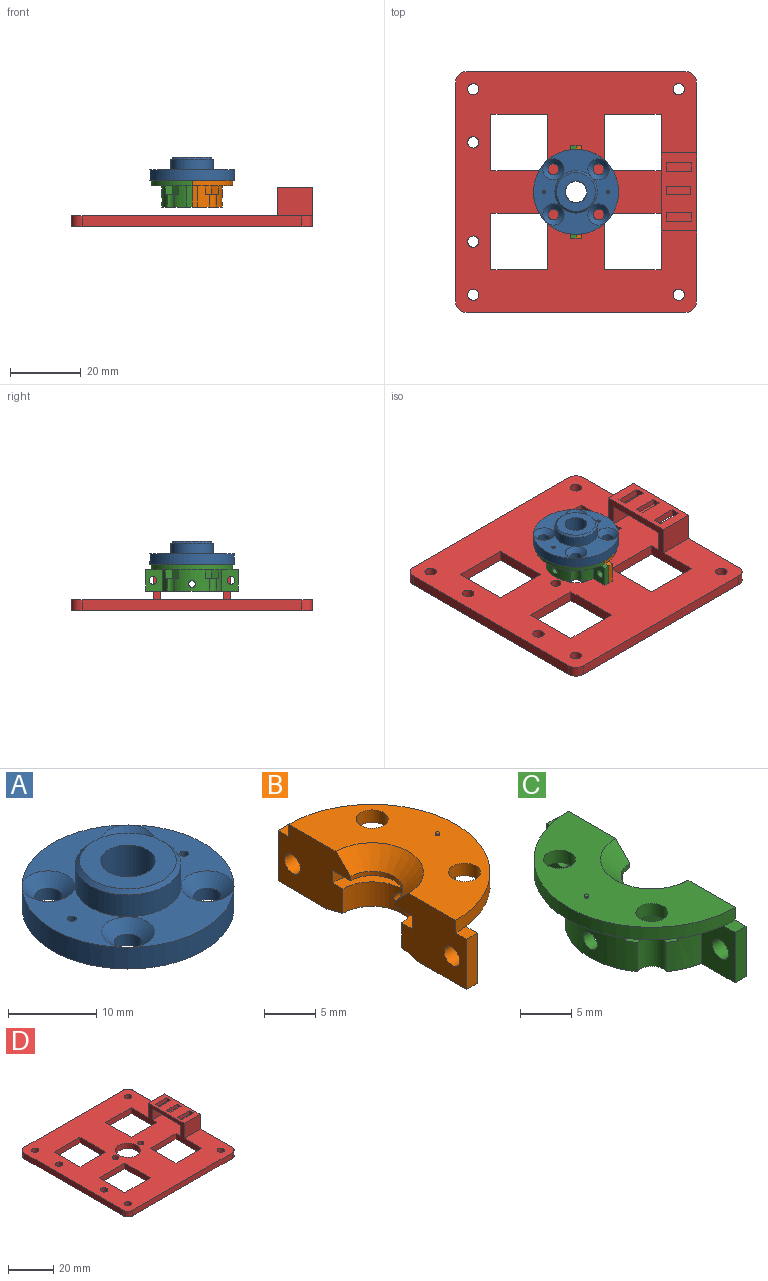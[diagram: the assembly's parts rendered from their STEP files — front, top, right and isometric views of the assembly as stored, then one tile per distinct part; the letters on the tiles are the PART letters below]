
ASSEMBLY  parts=4 mates=4
PART A: 18 faces, bbox 24x24x6.5 mm
  f0: cylinder r=3.1mm len=6.2mm, axis (0,0,-1), area 116.9mm2, adj f11,f13
  f1: cylinder r=1.6mm len=3.2mm, axis (0,0,-1), area 16.1mm2, adj f9,f17
  f2: cylinder r=1.6mm len=3.2mm, axis (0,0,-1), area 16.1mm2, adj f9,f16
  f3: cylinder r=1.6mm len=3.2mm, axis (0,0,-1), area 16.1mm2, adj f9,f15
  f4: cylinder r=1.6mm len=3.2mm, axis (0,0,-1), area 16.1mm2, adj f9,f14
  f5: cylinder r=0.5mm len=3mm, axis (0,0,-1), area 9.4mm2, adj f8,f9
  f6: cylinder r=0.5mm len=3mm, axis (0,0,-1), area 9.4mm2, adj f8,f9
  f7: cylinder r=12mm len=24mm, axis (0,0,-1), area 226.2mm2, adj f8,f9
  f8: plane 24x24mm, normal (0,0,1), area 225.6mm2, adj f5,f6,f7,f10,f14,f15,f16,f17
  f9: plane 24x24mm, normal (0,0,-1), area 377.9mm2, adj f1,f2,f3,f4,f5,f6,f7,f13
  f10: cylinder r=5.98mm len=11.95mm, axis (0,0,-1), area 112.6mm2, adj f8,f12
  f11: plane 10.95x10.95mm, normal (0,0,1), area 64mm2, adj f0,f12
  f12: cone r=5.47mm half-angle=45deg, axis (0,0,-1), area 25.4mm2, adj f10,f11
  f13: cone r=3.6mm half-angle=45deg, axis (0,0,-1), area 14.9mm2, adj f0,f9
  f14: cone r=1.6mm half-angle=45deg, axis (0,0,1), area 28.6mm2, adj f4,f8
  f15: cone r=1.6mm half-angle=45deg, axis (0,0,1), area 28.6mm2, adj f3,f8
  f16: cone r=1.6mm half-angle=45deg, axis (0,0,1), area 28.6mm2, adj f2,f8
  f17: cone r=1.6mm half-angle=45deg, axis (0,0,1), area 28.6mm2, adj f1,f8
PART B: 47 faces, bbox 11.5x26x7.9 mm
  f0: plane 4.29x4.29mm, normal (0,0,1), area 7.1mm2, adj f6,f7,f8,f14,f15,f16
  f1: plane 4.29x4.29mm, normal (0,0,1), area 7.1mm2, adj f3,f4,f5,f16,f17,f18
  f2: cylinder r=0.95mm len=1.9mm, axis (-1,0,0), area 7.3mm2, adj f16,f19
  f3: plane 2.5x2.04mm, normal (0.97,-0.26,0), area 5.3mm2, adj f1,f4,f18,f20
  f4: plane 2.5x2.25mm, normal (0.71,0.71,0), area 7.9mm2, adj f1,f3,f5,f20
  f5: plane 2.5x2.04mm, normal (-0.26,0.97,0), area 5.3mm2, adj f1,f4,f16,f20
  f6: plane 2.5x2.04mm, normal (-0.26,-0.97,0), area 5.3mm2, adj f0,f7,f16,f20
  f7: plane 2.5x2.25mm, normal (0.71,-0.71,0), area 7.9mm2, adj f0,f6,f8,f20
  f8: plane 2.5x2.04mm, normal (0.97,0.26,0), area 5.3mm2, adj f0,f7,f14,f20
  f9: cone r=0.2mm half-angle=45deg, axis (0,0,-1), area 0.2mm2, adj f23
  f10: cylinder r=0.95mm len=1.9mm, axis (-1,0,0), area 8.7mm2, adj f26,f40
  f11: plane 2.31x2.07mm, normal (0,0.87,-0.5), area 4.9mm2, adj f12,f19,f24,f26,f39
  f12: plane 2.37x1.88mm, normal (0,0,-1), area 4.2mm2, adj f11,f13,f19,f39
  f13: plane 2.31x2.07mm, normal (0,-0.87,-0.5), area 4.9mm2, adj f12,f19,f25,f26,f39
  f14: cylinder r=8.5mm len=6mm, axis (0,0,-1), area 19.3mm2, adj f0,f8,f15,f20,f37,f43
  f15: cylinder r=1.55mm len=3.5mm, axis (0,0,1), area 12.6mm2, adj f0,f14,f16,f37
  f16: cylinder r=8.5mm len=9.84mm, axis (0,0,-1), area 53.8mm2, adj f0,f1,f2,f5,f6,f15,f17,f20
  f17: cylinder r=1.55mm len=3.5mm, axis (0,0,1), area 12.6mm2, adj f1,f16,f18,f37
  f18: cylinder r=8.5mm len=6mm, axis (0,0,-1), area 19.3mm2, adj f1,f3,f17,f20,f37,f41
  f19: plane 4.73x4.05mm, normal (-1,0,0), area 13.9mm2, adj f2,f11,f12,f13,f24,f25,f37
  f20: plane 22.8x10mm, normal (0,0,-1), area 88.6mm2, adj f3,f4,f5,f6,f7,f8,f14,f16
  f21: cylinder r=1.55mm len=3.1mm, axis (0,0,1), area 14.6mm2, adj f20,f34
  f22: cylinder r=1.55mm len=3.1mm, axis (0,0,1), area 14.6mm2, adj f20,f34
  f23: cylinder r=0.2mm len=0.4mm, axis (0,0,-1), area 0.3mm2, adj f9,f34
  f24: plane 2.31x2.02mm, normal (0,1,0), area 4.5mm2, adj f11,f19,f26,f27,f37
  f25: plane 2.31x2.02mm, normal (0,-1,0), area 4.5mm2, adj f13,f19,f26,f27,f37
  f26: cylinder r=5.5mm len=4.73mm, axis (0,0,1), area 11.9mm2, adj f10,f11,f13,f24,f25,f27,f38
  f27: cone r=5.5mm half-angle=75.1deg, axis (0,0,-1), area 33mm2, adj f24,f25,f26,f37,f40,f45,f46
  f28: plane 1.6x1.5mm, normal (0,0,1), area 2.3mm2, adj f29,f35,f41,f45
  f29: plane 6x1.5mm, normal (0,1,0), area 9mm2, adj f28,f37,f41,f45
  f30: plane 1.6x1.5mm, normal (0,0,1), area 2.3mm2, adj f31,f35,f43,f46
  f31: plane 6x1.5mm, normal (0,-1,0), area 9mm2, adj f30,f37,f43,f46
  f32: cone r=3mm half-angle=45deg, axis (0,0,1), area 35.5mm2, adj f33,f34,f45,f46
  f33: cylinder r=3mm len=6mm, axis (0,0,1), area 4.7mm2, adj f32,f36,f45,f46
  f34: plane 23x11.5mm, normal (0,0,1), area 153.2mm2, adj f21,f22,f23,f32,f35,f45,f46
  f35: cylinder r=11.5mm len=23mm, axis (0,0,-1), area 54.2mm2, adj f20,f28,f30,f34,f45,f46
  f36: plane 11x5.5mm, normal (0,0,-1), area 33.4mm2, adj f33,f39,f45,f46
  f37: plane 26x8.5mm, normal (0,0,-1), area 56mm2, adj f14,f15,f16,f17,f18,f19,f24,f25
  f38: plane 11x5.5mm, normal (0,0,1), area 21.8mm2, adj f26,f39,f40,f45,f46
  f39: cylinder r=5.5mm len=11mm, axis (0,0,-1), area 24.4mm2, adj f11,f12,f13,f36,f38,f45,f46
  f40: cylinder r=4.05mm len=8.1mm, axis (0,0,1), area 34.2mm2, adj f10,f27,f38,f45,f46
  f41: plane 6x4.63mm, normal (1,0,0), area 24mm2, adj f18,f20,f28,f29,f37,f42
  f42: cylinder r=1.1mm len=2.2mm, axis (-1,0,0), area 10.4mm2, adj f41,f45
  f43: plane 6x4.63mm, normal (1,0,0), area 24mm2, adj f14,f20,f30,f31,f37,f44
  f44: cylinder r=1.1mm len=2.2mm, axis (-1,0,0), area 10.4mm2, adj f43,f46
  f45: plane 10x7.5mm, normal (-1,0,0), area 58.9mm2, adj f27,f28,f29,f32,f33,f34,f35,f36
  f46: plane 10x7.5mm, normal (-1,0,0), area 58.9mm2, adj f27,f30,f31,f32,f33,f34,f35,f36
PART C: 47 faces, bbox 11.5x26x7.9 mm
  f0: cylinder r=4.05mm len=8.1mm, axis (0,0,1), area 34.2mm2, adj f6,f7,f29,f45,f46
  f1: cylinder r=5.5mm len=11mm, axis (0,0,-1), area 24.4mm2, adj f3,f7,f23,f24,f25,f45,f46
  f2: plane 26x8.5mm, normal (0,0,-1), area 56mm2, adj f6,f9,f11,f17,f20,f21,f22,f26
  f3: plane 11x5.5mm, normal (0,0,-1), area 33.4mm2, adj f1,f8,f45,f46
  f4: cylinder r=11.5mm len=23mm, axis (0,0,-1), area 54.2mm2, adj f5,f10,f12,f16,f45,f46
  f5: plane 23x11.5mm, normal (0,0,1), area 153.2mm2, adj f4,f13,f18,f19,f43,f45,f46
  f6: cone r=5.5mm half-angle=75.1deg, axis (0,0,-1), area 33mm2, adj f0,f2,f26,f27,f28,f45,f46
  f7: plane 11x5.5mm, normal (0,0,1), area 21.8mm2, adj f0,f1,f28,f45,f46
  f8: cylinder r=3mm len=6mm, axis (0,0,1), area 4.7mm2, adj f3,f13,f45,f46
  f9: plane 6x1.5mm, normal (0,1,0), area 9mm2, adj f2,f10,f41,f45
  f10: plane 1.6x1.5mm, normal (0,0,1), area 2.3mm2, adj f4,f9,f41,f45
  f11: plane 6x1.5mm, normal (0,-1,0), area 9mm2, adj f2,f12,f42,f46
  f12: plane 1.6x1.5mm, normal (0,0,1), area 2.3mm2, adj f4,f11,f42,f46
  f13: cone r=3mm half-angle=45deg, axis (0,0,1), area 35.5mm2, adj f5,f8,f45,f46
  f14: cylinder r=1.1mm len=2.2mm, axis (-1,0,0), area 10.4mm2, adj f42,f46
  f15: cylinder r=1.1mm len=2.2mm, axis (-1,0,0), area 10.4mm2, adj f41,f45
  f16: plane 22.8x10mm, normal (0,0,-1), area 88.6mm2, adj f4,f17,f18,f19,f20,f21,f33,f34
  f17: cylinder r=8.5mm len=6mm, axis (0,0,-1), area 19.3mm2, adj f2,f16,f32,f34,f35,f42
  f18: cylinder r=1.55mm len=3.1mm, axis (0,0,1), area 14.6mm2, adj f5,f16
  f19: cylinder r=1.55mm len=3.1mm, axis (0,0,1), area 14.6mm2, adj f5,f16
  f20: cylinder r=8.5mm len=9.84mm, axis (0,0,-1), area 53.8mm2, adj f2,f16,f30,f31,f32,f33,f35,f38
  f21: cylinder r=8.5mm len=6mm, axis (0,0,-1), area 19.3mm2, adj f2,f16,f31,f37,f39,f41
  f22: plane 4.73x4.05mm, normal (1,0,0), area 13.9mm2, adj f2,f23,f24,f25,f26,f27,f30
  f23: plane 2.31x2.07mm, normal (0,0.87,-0.5), area 4.9mm2, adj f1,f22,f25,f26,f28
  f24: plane 2.31x2.07mm, normal (0,-0.87,-0.5), area 4.9mm2, adj f1,f22,f25,f27,f28
  f25: plane 2.37x1.88mm, normal (0,0,-1), area 4.2mm2, adj f1,f22,f23,f24
  f26: plane 2.31x2.02mm, normal (0,1,0), area 4.5mm2, adj f2,f6,f22,f23,f28
  f27: plane 2.31x2.02mm, normal (0,-1,0), area 4.5mm2, adj f2,f6,f22,f24,f28
  f28: cylinder r=5.5mm len=4.73mm, axis (0,0,1), area 11.9mm2, adj f6,f7,f23,f24,f26,f27,f29
  f29: cylinder r=0.95mm len=1.9mm, axis (-1,0,0), area 8.7mm2, adj f0,f28
  f30: cylinder r=0.95mm len=1.9mm, axis (-1,0,0), area 7.3mm2, adj f20,f22
  f31: cylinder r=1.55mm len=3.5mm, axis (0,0,1), area 12.6mm2, adj f2,f20,f21,f39
  f32: cylinder r=1.55mm len=3.5mm, axis (0,0,1), area 12.6mm2, adj f2,f17,f20,f35
  f33: plane 2.5x2.04mm, normal (0.26,-0.97,0), area 5.3mm2, adj f16,f20,f35,f36
  f34: plane 2.5x2.04mm, normal (-0.97,0.26,0), area 5.3mm2, adj f16,f17,f35,f36
  f35: plane 4.29x4.29mm, normal (0,0,1), area 7.1mm2, adj f17,f20,f32,f33,f34,f36
  f36: plane 2.5x2.25mm, normal (-0.71,-0.71,0), area 7.9mm2, adj f16,f33,f34,f35
  f37: plane 2.5x2.04mm, normal (-0.97,-0.26,0), area 5.3mm2, adj f16,f21,f39,f40
  f38: plane 2.5x2.04mm, normal (0.26,0.97,0), area 5.3mm2, adj f16,f20,f39,f40
  f39: plane 4.29x4.29mm, normal (0,0,1), area 7.1mm2, adj f20,f21,f31,f37,f38,f40
  f40: plane 2.5x2.25mm, normal (-0.71,0.71,0), area 7.9mm2, adj f16,f37,f38,f39
  f41: plane 6x4.63mm, normal (-1,0,0), area 24mm2, adj f2,f9,f10,f15,f16,f21
  f42: plane 6x4.63mm, normal (-1,0,0), area 24mm2, adj f2,f11,f12,f14,f16,f17
  f43: cylinder r=0.2mm len=0.4mm, axis (0,0,-1), area 0.3mm2, adj f5,f44
  f44: cone r=0.2mm half-angle=45deg, axis (0,0,-1), area 0.2mm2, adj f43
  f45: plane 10x7.5mm, normal (1,0,0), area 58.9mm2, adj f0,f1,f2,f3,f4,f5,f6,f7
  f46: plane 10x7.5mm, normal (1,0,0), area 58.9mm2, adj f0,f1,f2,f3,f4,f5,f6,f7
PART D: 54 faces, bbox 68x68x11 mm
  f0: plane 22x10mm, normal (0,0,1), area 168.5mm2, adj f3,f13,f37,f40,f41,f42,f43,f44
  f1: plane 18x10mm, normal (0,0,-1), area 144.1mm2, adj f3,f13,f36,f38,f41,f42,f43,f44
  f2: plane 68x68mm, normal (0,0,1), area 3396.7mm2, adj f3,f4,f5,f6,f7,f8,f9,f10
  f3: plane 62x11mm, normal (1,0,0), area 254mm2, adj f0,f1,f2,f4,f34,f35,f36,f37
  f4: cylinder r=3mm len=3mm, axis (0,0,-1), area 14.1mm2, adj f2,f3,f5,f35
  f5: plane 62x3mm, normal (0,1,0), area 186mm2, adj f2,f4,f6,f35
  f6: cylinder r=3mm len=3mm, axis (0,0,-1), area 14.1mm2, adj f2,f5,f7,f35
  f7: plane 62x3mm, normal (-1,0,0), area 186mm2, adj f2,f6,f8,f35
  f8: cylinder r=3mm len=3mm, axis (0,0,-1), area 14.1mm2, adj f2,f7,f9,f35
  f9: plane 62x3mm, normal (0,-1,0), area 186mm2, adj f2,f8,f34,f35
  f10: plane 16x3mm, normal (1,0,0), area 48mm2, adj f2,f11,f22,f35
  f11: plane 16x3mm, normal (0,-1,0), area 48mm2, adj f2,f10,f12,f35
  f12: plane 16x3mm, normal (-1,0,0), area 48mm2, adj f2,f11,f22,f35
  f13: plane 44x11mm, normal (-1,0,0), area 164mm2, adj f0,f1,f2,f14,f16,f18,f23,f35
  f14: plane 16x3mm, normal (0,1,0), area 48mm2, adj f2,f13,f15,f35
  f15: plane 16x3mm, normal (1,0,0), area 48mm2, adj f2,f14,f23,f35
  f16: plane 16x3mm, normal (0,1,0), area 48mm2, adj f2,f13,f17,f35
  f17: plane 16x3mm, normal (1,0,0), area 48mm2, adj f2,f16,f18,f35
  f18: plane 16x3mm, normal (0,-1,0), area 48mm2, adj f2,f13,f17,f35
  f19: plane 16x3mm, normal (0,1,0), area 48mm2, adj f2,f20,f33,f35
  f20: plane 16x3mm, normal (1,0,0), area 48mm2, adj f2,f19,f21,f35
  f21: plane 16x3mm, normal (0,-1,0), area 48mm2, adj f2,f20,f33,f35
  f22: plane 16x3mm, normal (0,1,0), area 48mm2, adj f2,f10,f12,f35
  f23: plane 16x3mm, normal (0,-1,0), area 48mm2, adj f2,f13,f15,f35
  f24: cylinder r=1.4mm len=3mm, axis (0,0,-1), area 26.4mm2, adj f2,f35
  f25: cylinder r=1.4mm len=3mm, axis (0,0,-1), area 26.4mm2, adj f2,f35
  f26: cylinder r=5.5mm len=11mm, axis (0,0,-1), area 103.7mm2, adj f2,f35
  f27: cylinder r=1.6mm len=3.2mm, axis (0,0,-1), area 30.2mm2, adj f2,f35
  f28: cylinder r=1.6mm len=3.2mm, axis (0,0,-1), area 30.2mm2, adj f2,f35
  f29: cylinder r=1.6mm len=3.2mm, axis (0,0,-1), area 30.2mm2, adj f2,f35
  f30: cylinder r=1.6mm len=3.2mm, axis (0,0,-1), area 30.2mm2, adj f2,f35
  f31: cylinder r=1.6mm len=3.2mm, axis (0,0,-1), area 30.2mm2, adj f2,f35
  f32: cylinder r=1.6mm len=3.2mm, axis (0,0,-1), area 30.2mm2, adj f2,f35
  f33: plane 16x3mm, normal (-1,0,0), area 48mm2, adj f2,f19,f21,f35
  f34: cylinder r=3mm len=3mm, axis (0,0,-1), area 14.1mm2, adj f2,f3,f9,f35
  f35: plane 68x68mm, normal (0,0,-1), area 3436.7mm2, adj f3,f4,f5,f6,f7,f8,f9,f10
  f36: plane 10x6mm, normal (0,1,0), area 60mm2, adj f1,f2,f3,f13
  f37: plane 10x8mm, normal (0,-1,0), area 80mm2, adj f0,f2,f3,f13
  f38: plane 10x6mm, normal (0,-1,0), area 60mm2, adj f1,f2,f3,f13
  f39: plane 10x6mm, normal (0,1,0), area 60mm2, adj f2,f3,f13,f40
  f40: plane 10x2mm, normal (0,1,0), area 20mm2, adj f0,f3,f13,f39
  f41: plane 7.17x2mm, normal (0,-1,0), area 14.3mm2, adj f0,f1,f42,f44
  f42: plane 2.5x2mm, normal (1,0,0), area 5mm2, adj f0,f1,f41,f43
  f43: plane 7.17x2mm, normal (0,1,0), area 14.3mm2, adj f0,f1,f42,f44
  f44: plane 2.5x2mm, normal (-1,0,0), area 5mm2, adj f0,f1,f41,f43
  f45: plane 7.17x2mm, normal (0,-1,0), area 14.3mm2, adj f0,f1,f46,f48
  f46: plane 2.5x2mm, normal (1,0,0), area 5mm2, adj f0,f1,f45,f47
  f47: plane 7.17x2mm, normal (0,1,0), area 14.3mm2, adj f0,f1,f46,f48
  f48: plane 2.5x2mm, normal (-1,0,0), area 5mm2, adj f0,f1,f45,f47
  f49: plane 6.8x1.5mm, normal (0,-1,0), area 10.2mm2, adj f0,f50,f52,f53
  f50: plane 2.29x1.5mm, normal (1,0,0), area 3.4mm2, adj f0,f49,f51,f53
  f51: plane 6.8x1.5mm, normal (0,1,0), area 10.2mm2, adj f0,f50,f52,f53
  f52: plane 2.29x1.5mm, normal (-1,0,0), area 3.4mm2, adj f0,f49,f51,f53
  f53: plane 6.8x2.29mm, normal (0,0,1), area 15.6mm2, adj f49,f50,f51,f52
PLACE A t=(-2.18,-5.56,-4.5)mm
PLACE B t=(-2.18,-5.56,-12)mm
PLACE C t=(-2.18,-5.56,-12)mm
PLACE D t=(-2.18,-5.56,-17.5)mm
MATE planar B.f46 <-> C.f46  axis (-1,0,0) through (-2.18,-13.9,-8.29)mm
MATE revolute C.f0 <-> D.f26  axis (0,0,1) through (-2.18,-5.56,-8.5)mm
MATE fastened B.f44 <-> C.f14  axis (-1,0,0) through (-2.18,-16.56,-9)mm
MATE fastened A.f6 <-> B.f9  axis (0,0,-1) through (6.82,-5.56,-4.5)mm
